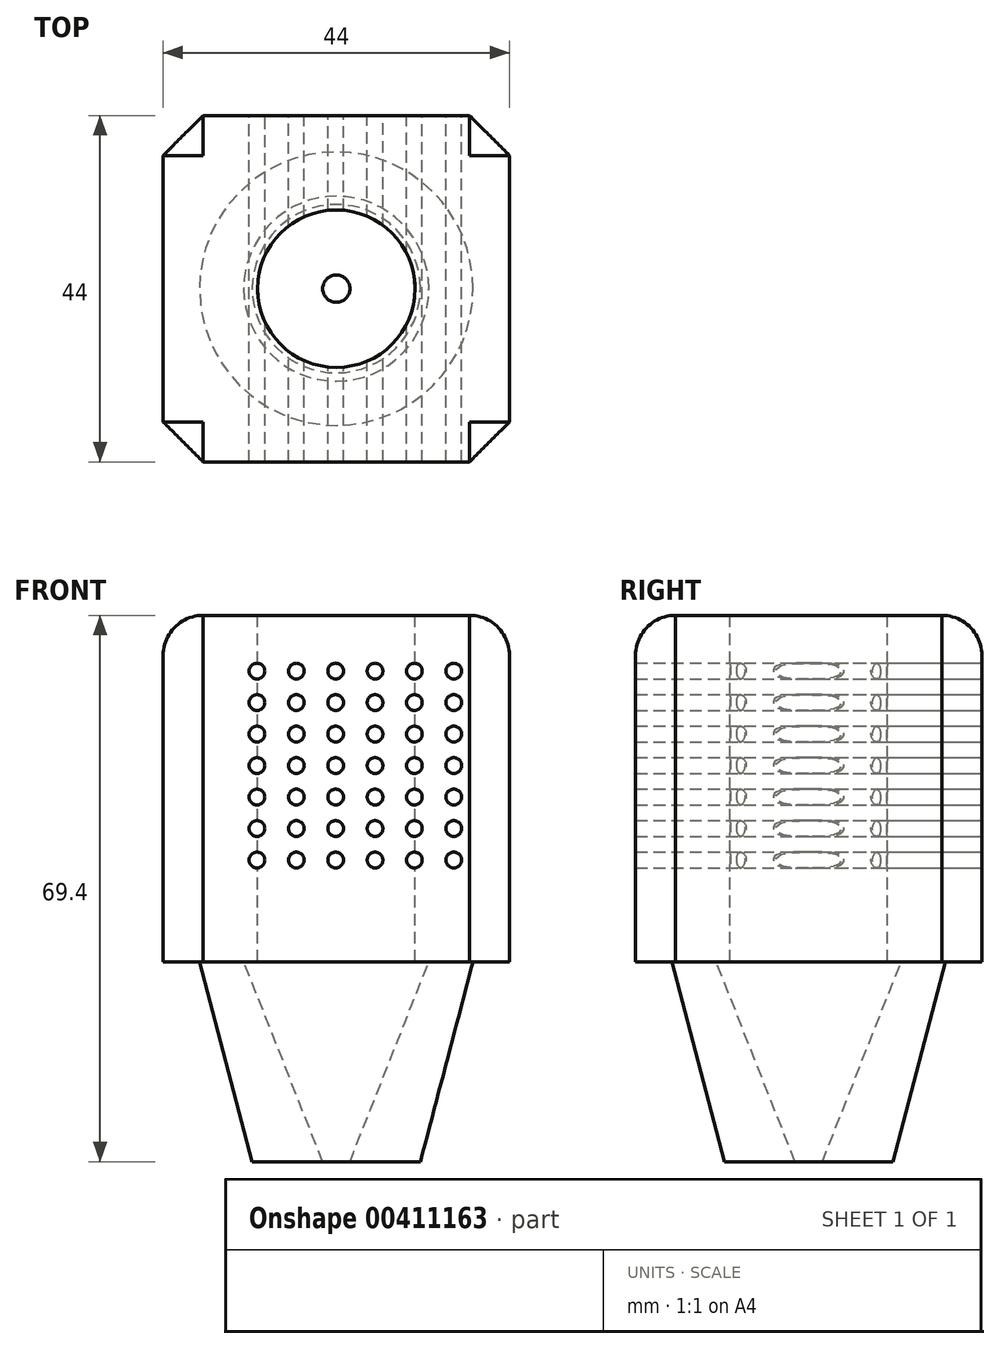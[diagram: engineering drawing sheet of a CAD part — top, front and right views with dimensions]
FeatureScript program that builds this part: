
annotation { "Feature Type Name" : "Feature", "Feature Type Description" : "" }
export const myFeature = defineFeature(function(context is Context, id is Id, definition is map)
    precondition{}
    {
        {
            var Q0;
            Q0=qCreatedBy(makeId("Top.planeOp"),FACE);
            var sketch = newSketch(context, id + "F0", { "sketchPlane" : qUnion([Q0])});
            skLineSegment(sketch, "E0.bottom", {"start": v(-22, -22) * mm, "end": v(22, -22) * mm});
            skLineSegment(sketch, "E0.top", {"start": v(-22, 22) * mm, "end": v(22, 22) * mm});
            skLineSegment(sketch, "E0.left", {"start": v(-22, -22) * mm, "end": v(-22, 22) * mm});
            skLineSegment(sketch, "E0.right", {"start": v(22, -22) * mm, "end": v(22, 22) * mm});
            skPoint(sketch, "E0.middle", {"position": v(0, 0) * mm});
            skSolve(sketch);
        }
        {
            var Q0;
            Q0 = qSketchRegion(id + "F0", true);
            extrude(context, id + "F1", {"entities" : qUnion([Q0]), "depth" : 44 * mm});
        }
        {
            var Q0;
            Q0=makeQuery(id+"F1.opExtrude","CAP_EDGE",EDGE,{"disambiguationData":[OSD([sQuery(id+"F0.wireOp",EDGE,"E0.right")])],"isStart":false});
            var Q1;
            Q1=makeQuery(id+"F1.opExtrude","CAP_EDGE",EDGE,{"disambiguationData":[OSD([sQuery(id+"F0.wireOp",EDGE,"E0.bottom")])],"isStart":false});
            var Q2;
            Q2=makeQuery(id+"F1.opExtrude","CAP_FACE",FACE,{"disambiguationData":[OSD([sQuery(id+"F0.wireOp",EDGE,"E0.bottom"),sQuery(id+"F0.wireOp",EDGE,"E0.top"),sQuery(id+"F0.wireOp",EDGE,"E0.left"),sQuery(id+"F0.wireOp",EDGE,"E0.right")])],"isStart":false});
            fillet(context, id + "F2", {"entities" : qUnion([Q0, Q1, Q2]), "radius" : 5.08 * mm, "tangentPropagation" : true, "allowEdgeOverflow" : false});
        }
        {
            var Q0;
            Q0=makeQuery(id+"F1.opExtrude","CAP_FACE",FACE,{"disambiguationData":[OSD([sQuery(id+"F0.wireOp",EDGE,"E0.bottom"),sQuery(id+"F0.wireOp",EDGE,"E0.top"),sQuery(id+"F0.wireOp",EDGE,"E0.left"),sQuery(id+"F0.wireOp",EDGE,"E0.right")])],"isStart":false});
            var sketch = newSketch(context, id + "F3", { "sketchPlane" : qUnion([Q0])});
            skLineSegment(sketch, "E1", {"start": v(-16.92, 16.92) * mm, "end": v(16.92, -16.92) * mm});
            skCircle(sketch, "E2", {"center": v(0, 0) * mm, "radius": 10 * mm});
            skSolve(sketch);
        }
        {
            var Q0;
            Q0 = qSketchRegion(id + "F3", true);
            extrude(context, id + "F4", {"entities" : qUnion([Q0]), "operationType" : NewBodyOperationType.REMOVE, "oppositeDirection" : true, "depth" : 44 * mm});
        }
        {
            var Q0;
            Q0=makeQuery(id+"F1.opExtrude","SWEPT_EDGE",EDGE,{"disambiguationData":[OSD([sQuery(id+"F0.wireOp",EDGE,"E0.bottom"),sQuery(id+"F0.wireOp",EDGE,"E0.left")])]});
            var Q1;
            Q1=makeQuery(id+"F1.opExtrude","SWEPT_EDGE",EDGE,{"disambiguationData":[OSD([sQuery(id+"F0.wireOp",EDGE,"E0.bottom"),sQuery(id+"F0.wireOp",EDGE,"E0.right")])]});
            var Q2;
            Q2=makeQuery(id+"F1.opExtrude","SWEPT_EDGE",EDGE,{"disambiguationData":[OSD([sQuery(id+"F0.wireOp",EDGE,"E0.top"),sQuery(id+"F0.wireOp",EDGE,"E0.left")])]});
            var Q3;
            Q3=makeQuery(id+"F1.opExtrude","SWEPT_EDGE",EDGE,{"disambiguationData":[OSD([sQuery(id+"F0.wireOp",EDGE,"E0.top"),sQuery(id+"F0.wireOp",EDGE,"E0.right")])]});
            chamfer(context, id + "F5", {"entities" : qUnion([Q0, Q1, Q2, Q3]), "width" : 5.08 * mm, "tangentPropagation" : true});
        }
        {
            var Q0;
            Q0=makeQuery(id+"F1.opExtrude","SWEPT_FACE",FACE,{"disambiguationData":[OSD([sQuery(id+"F0.wireOp",EDGE,"E0.top")])]});
            var sketch = newSketch(context, id + "F6", { "sketchPlane" : qUnion([Q0])});
            skCircle(sketch, "E3", {"center": v(-14.92, 36.92) * mm, "radius": 1 * mm});
            skCircle(sketch, "E4.0.1.0", {"center": v(-14.92, 32.92) * mm, "radius": 1 * mm});
            skCircle(sketch, "E4.0.2.0", {"center": v(-14.92, 28.92) * mm, "radius": 1 * mm});
            skCircle(sketch, "E4.0.3.0", {"center": v(-14.92, 24.92) * mm, "radius": 1 * mm});
            skCircle(sketch, "E4.0.4.0", {"center": v(-14.92, 20.92) * mm, "radius": 1 * mm});
            skCircle(sketch, "E4.0.5.0", {"center": v(-14.92, 16.92) * mm, "radius": 1 * mm});
            skCircle(sketch, "E4.0.6.0", {"center": v(-14.92, 12.92) * mm, "radius": 1 * mm});
            skCircle(sketch, "E4.1.0.0", {"center": v(-9.92, 36.92) * mm, "radius": 1 * mm});
            skCircle(sketch, "E4.1.1.0", {"center": v(-9.92, 32.92) * mm, "radius": 1 * mm});
            skCircle(sketch, "E4.1.2.0", {"center": v(-9.92, 28.92) * mm, "radius": 1 * mm});
            skCircle(sketch, "E4.1.3.0", {"center": v(-9.92, 24.92) * mm, "radius": 1 * mm});
            skCircle(sketch, "E4.1.4.0", {"center": v(-9.92, 20.92) * mm, "radius": 1 * mm});
            skCircle(sketch, "E4.1.5.0", {"center": v(-9.92, 16.92) * mm, "radius": 1 * mm});
            skCircle(sketch, "E4.1.6.0", {"center": v(-9.92, 12.92) * mm, "radius": 1 * mm});
            skCircle(sketch, "E4.2.0.0", {"center": v(-4.92, 36.92) * mm, "radius": 1 * mm});
            skCircle(sketch, "E4.2.1.0", {"center": v(-4.92, 32.92) * mm, "radius": 1 * mm});
            skCircle(sketch, "E4.2.2.0", {"center": v(-4.92, 28.92) * mm, "radius": 1 * mm});
            skCircle(sketch, "E4.2.3.0", {"center": v(-4.92, 24.92) * mm, "radius": 1 * mm});
            skCircle(sketch, "E4.2.4.0", {"center": v(-4.92, 20.92) * mm, "radius": 1 * mm});
            skCircle(sketch, "E4.2.5.0", {"center": v(-4.92, 16.92) * mm, "radius": 1 * mm});
            skCircle(sketch, "E4.2.6.0", {"center": v(-4.92, 12.92) * mm, "radius": 1 * mm});
            skCircle(sketch, "E4.3.0.0", {"center": v(0.08, 36.92) * mm, "radius": 1 * mm});
            skCircle(sketch, "E4.3.1.0", {"center": v(0.08, 32.92) * mm, "radius": 1 * mm});
            skCircle(sketch, "E4.3.2.0", {"center": v(0.08, 28.92) * mm, "radius": 1 * mm});
            skCircle(sketch, "E4.3.3.0", {"center": v(0.08, 24.92) * mm, "radius": 1 * mm});
            skCircle(sketch, "E4.3.4.0", {"center": v(0.08, 20.92) * mm, "radius": 1 * mm});
            skCircle(sketch, "E4.3.5.0", {"center": v(0.08, 16.92) * mm, "radius": 1 * mm});
            skCircle(sketch, "E4.3.6.0", {"center": v(0.08, 12.92) * mm, "radius": 1 * mm});
            skCircle(sketch, "E4.4.0.0", {"center": v(5.08, 36.92) * mm, "radius": 1 * mm});
            skCircle(sketch, "E4.4.1.0", {"center": v(5.08, 32.92) * mm, "radius": 1 * mm});
            skCircle(sketch, "E4.4.2.0", {"center": v(5.08, 28.92) * mm, "radius": 1 * mm});
            skCircle(sketch, "E4.4.3.0", {"center": v(5.08, 24.92) * mm, "radius": 1 * mm});
            skCircle(sketch, "E4.4.4.0", {"center": v(5.08, 20.92) * mm, "radius": 1 * mm});
            skCircle(sketch, "E4.4.5.0", {"center": v(5.08, 16.92) * mm, "radius": 1 * mm});
            skCircle(sketch, "E4.4.6.0", {"center": v(5.08, 12.92) * mm, "radius": 1 * mm});
            skCircle(sketch, "E4.5.0.0", {"center": v(10.08, 36.92) * mm, "radius": 1 * mm});
            skCircle(sketch, "E4.5.1.0", {"center": v(10.08, 32.92) * mm, "radius": 1 * mm});
            skCircle(sketch, "E4.5.2.0", {"center": v(10.08, 28.92) * mm, "radius": 1 * mm});
            skCircle(sketch, "E4.5.3.0", {"center": v(10.08, 24.92) * mm, "radius": 1 * mm});
            skCircle(sketch, "E4.5.4.0", {"center": v(10.08, 20.92) * mm, "radius": 1 * mm});
            skCircle(sketch, "E4.5.5.0", {"center": v(10.08, 16.92) * mm, "radius": 1 * mm});
            skCircle(sketch, "E4.5.6.0", {"center": v(10.08, 12.92) * mm, "radius": 1 * mm});
            skLineSegment(sketch, "E4.direction1", {"start": v(-14.92, 36.92) * mm, "end": v(-9.92, 36.92) * mm, "construction": true});
            skLineSegment(sketch, "E4.direction2", {"start": v(-14.92, 36.92) * mm, "end": v(-14.92, 32.92) * mm, "construction": true});
            skSolve(sketch);
        }
        {
            var Q0;
            Q0 = qSketchRegion(id + "F6", true);
            extrude(context, id + "F7", {"entities" : qUnion([Q0]), "operationType" : NewBodyOperationType.REMOVE, "oppositeDirection" : true, "depth" : 50.8 * mm});
        }
        {
            var Q0;
            Q0=qCreatedBy(makeId("Right.planeOp"),FACE);
            var sketch = newSketch(context, id + "F8", { "sketchPlane" : qUnion([Q0])});
            skLineSegment(sketch, "E5", {"start": v(-10.69, -25.4) * mm, "end": v(-17.36, 0) * mm});
            skLineSegment(sketch, "E6", {"start": v(-17.36, 0) * mm, "end": v(-11.75, 0) * mm});
            skLineSegment(sketch, "E7", {"start": v(-11.75, 0) * mm, "end": v(-1.73, -25.4) * mm});
            skLineSegment(sketch, "E8", {"start": v(-10.69, -25.4) * mm, "end": v(-1.73, -25.4) * mm});
            skLineSegment(sketch, "E9", {"start": v(0, 0) * mm, "end": v(0, -17.26) * mm});
            skSolve(sketch);
        }
        {
            var Q0;
            Q0=makeQuery(id+"F8.imprint","IMPRINT",FACE,{"disambiguationData":[TD([[makeQuery(id+"F8.imprint","IMPRINT",EDGE,{"derivedFrom":sQuery(id+"F8.wireOp",EDGE,"E5")}),-1.0]])]});
            var Q1;
            Q1=sQuery(id+"F8.wireOp",EDGE,"E9");
            revolve(context, id + "F9", {"operationType" : NewBodyOperationType.ADD, "entities" : qUnion([Q0]), "axis" : qUnion([Q1]), "revolveType" : RevolveType.FULL});
        }
    });
